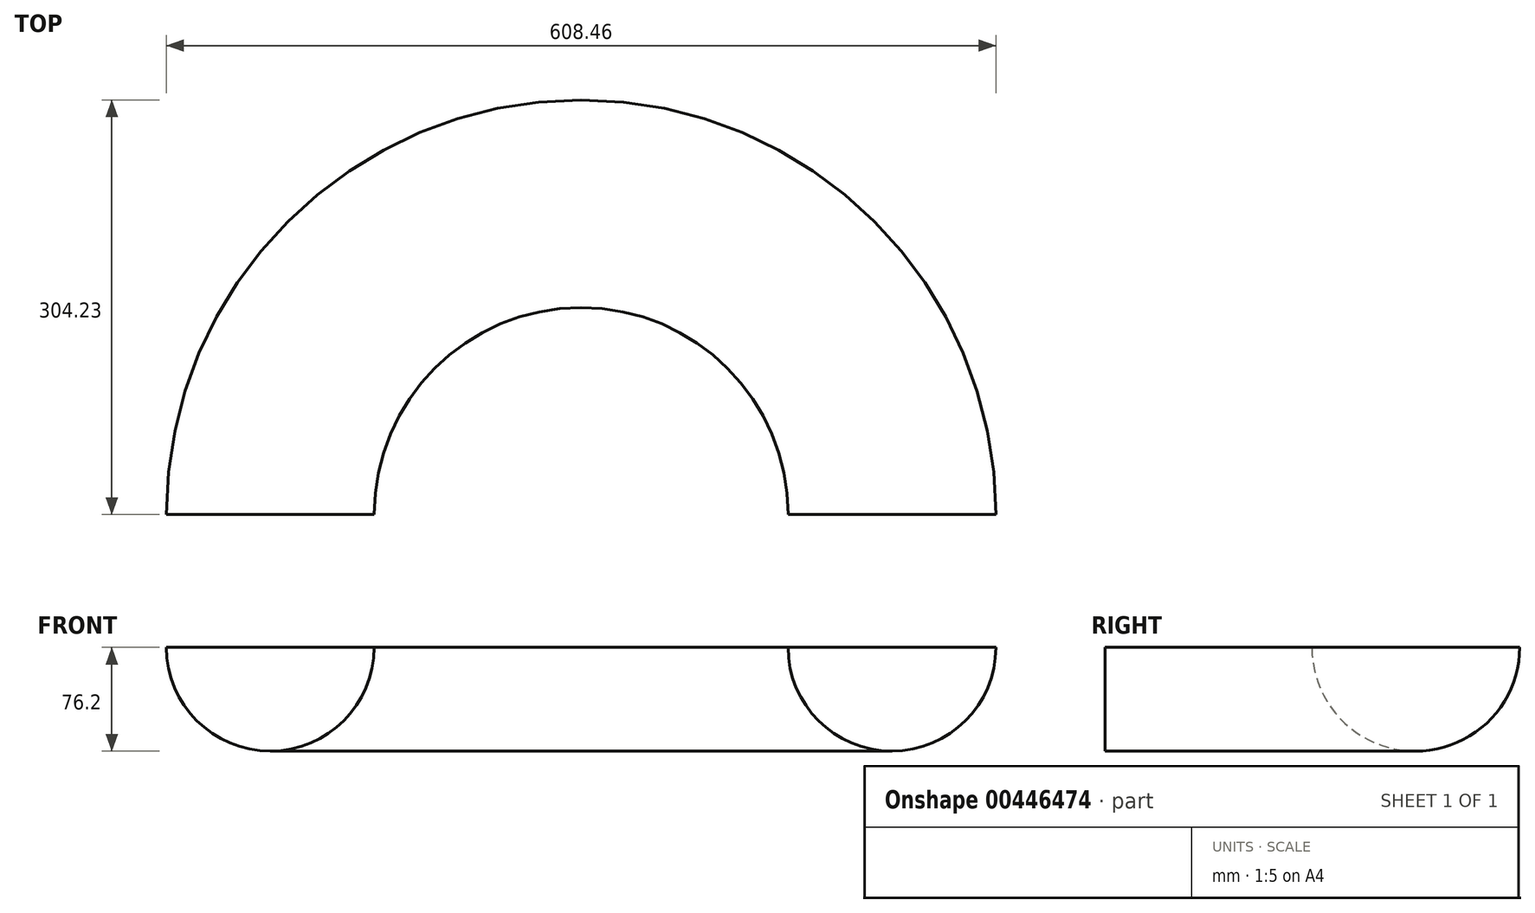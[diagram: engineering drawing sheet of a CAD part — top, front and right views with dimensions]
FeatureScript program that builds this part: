
annotation { "Feature Type Name" : "Feature", "Feature Type Description" : "" }
export const myFeature = defineFeature(function(context is Context, id is Id, definition is map)
    precondition{}
    {
        {
            var Q0;
            Q0=qCreatedBy(makeId("Top.planeOp"),FACE);
            var sketch = newSketch(context, id + "F0", { "sketchPlane" : qUnion([Q0])});
            skArc(sketch, "E0", {"start": v(-228.6, 0) * mm, "mid": v(0, 228.6) * mm, "end": v(228.6, 0) * mm});
            skSolve(sketch);
        }
        {
            var Q0;
            Q0=qCreatedBy(makeId("Front.planeOp"),FACE);
            var sketch = newSketch(context, id + "F1", { "sketchPlane" : qUnion([Q0])});
            skArc(sketch, "E1", {"start": v(-304.23, 0) * mm, "mid": v(-228.03, -76.2) * mm, "end": v(-151.83, 0) * mm});
            skLineSegment(sketch, "E2", {"start": v(-304.23, 0) * mm, "end": v(-151.83, 0) * mm});
            skSolve(sketch);
        }
        {
            var Q0;
            Q0=makeQuery(id+"F1.imprint","IMPRINT",FACE,{"disambiguationData":[TD([[makeQuery(id+"F1.imprint","IMPRINT",EDGE,{"derivedFrom":sQuery(id+"F1.wireOp",EDGE,"E1")}),1.0]])]});
            var Q1;
            Q1=sQuery(id+"F0.wireOp",EDGE,"E0");
            sweep(context, id + "F2", {"profiles" : qUnion([Q0]), "path" : qUnion([Q1])});
        }
    });
